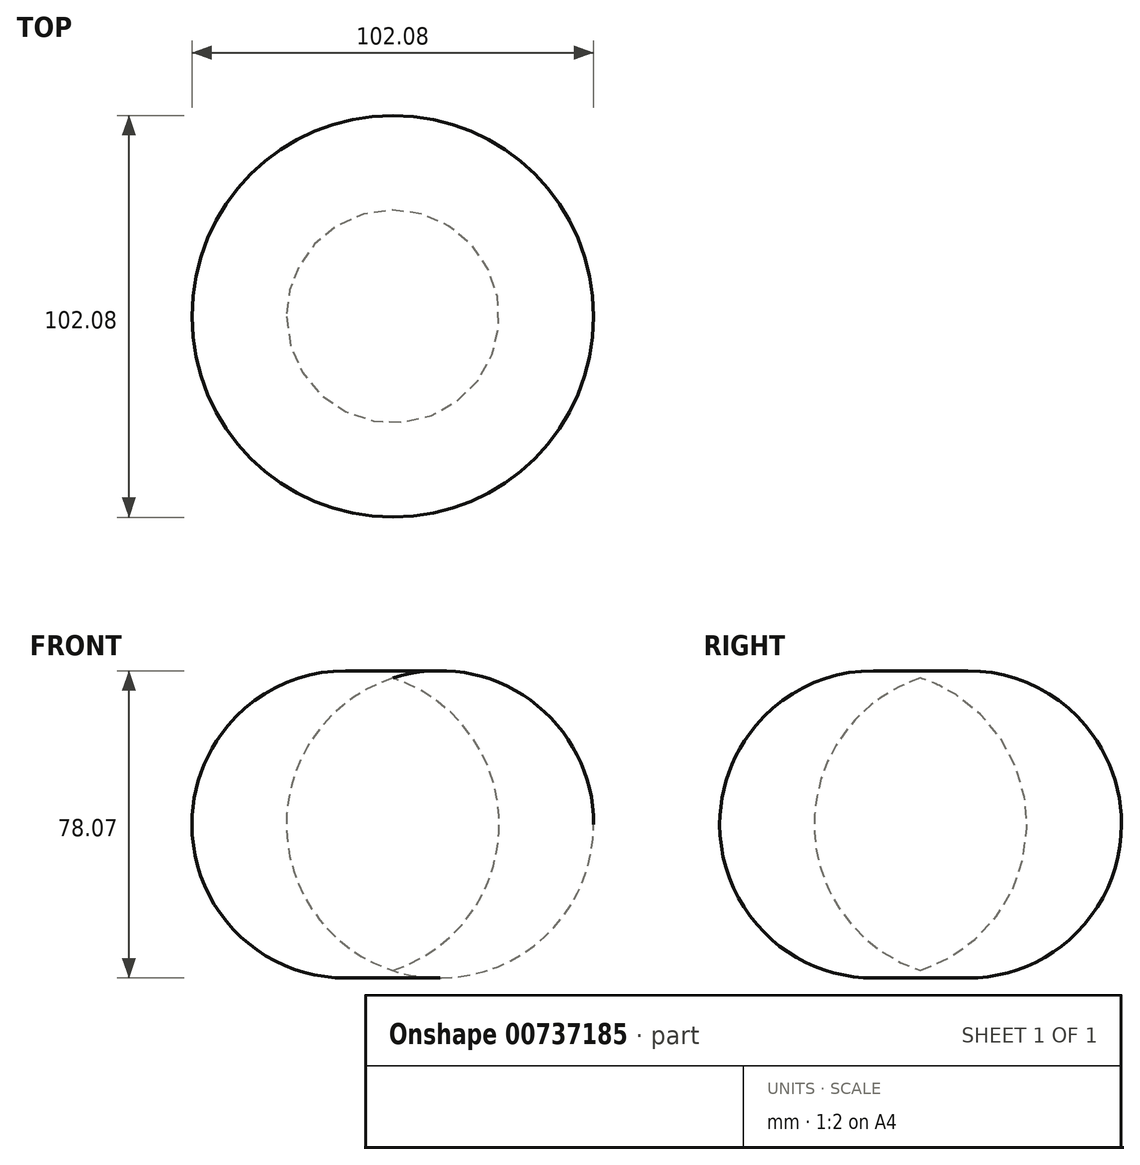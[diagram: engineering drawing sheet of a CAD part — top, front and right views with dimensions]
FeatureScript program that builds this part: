
annotation { "Feature Type Name" : "Feature", "Feature Type Description" : "" }
export const myFeature = defineFeature(function(context is Context, id is Id, definition is map)
    precondition{}
    {
        {
            var Q0;
            Q0=qCreatedBy(makeId("Front.planeOp"),FACE);
            var sketch = newSketch(context, id + "F0", { "sketchPlane" : qUnion([Q0])});
            skArc(sketch, "E0", {"start": v(0, -36.37) * mm, "mid": v(27.03, 0.78) * mm, "end": v(0, 37.92) * mm});
            skLineSegment(sketch, "E1", {"start": v(0, 37.92) * mm, "end": v(0, -36.37) * mm});
            skSolve(sketch);
        }
        {
            var Q0;
            Q0=makeQuery(id+"F0.imprint","IMPRINT",FACE,{"disambiguationData":[TD([[makeQuery(id+"F0.imprint","IMPRINT",EDGE,{"derivedFrom":sQuery(id+"F0.wireOp",EDGE,"E0")}),1.0]])]});
            var Q1;
            Q1=sQuery(id+"F0.wireOp",EDGE,"E1");
            revolve(context, id + "F1", {"surfaceOperationType" : NewSurfaceOperationType.NEW, "entities" : qUnion([Q0]), "axis" : qUnion([Q1]), "revolveType" : RevolveType.FULL});
        }
    });
